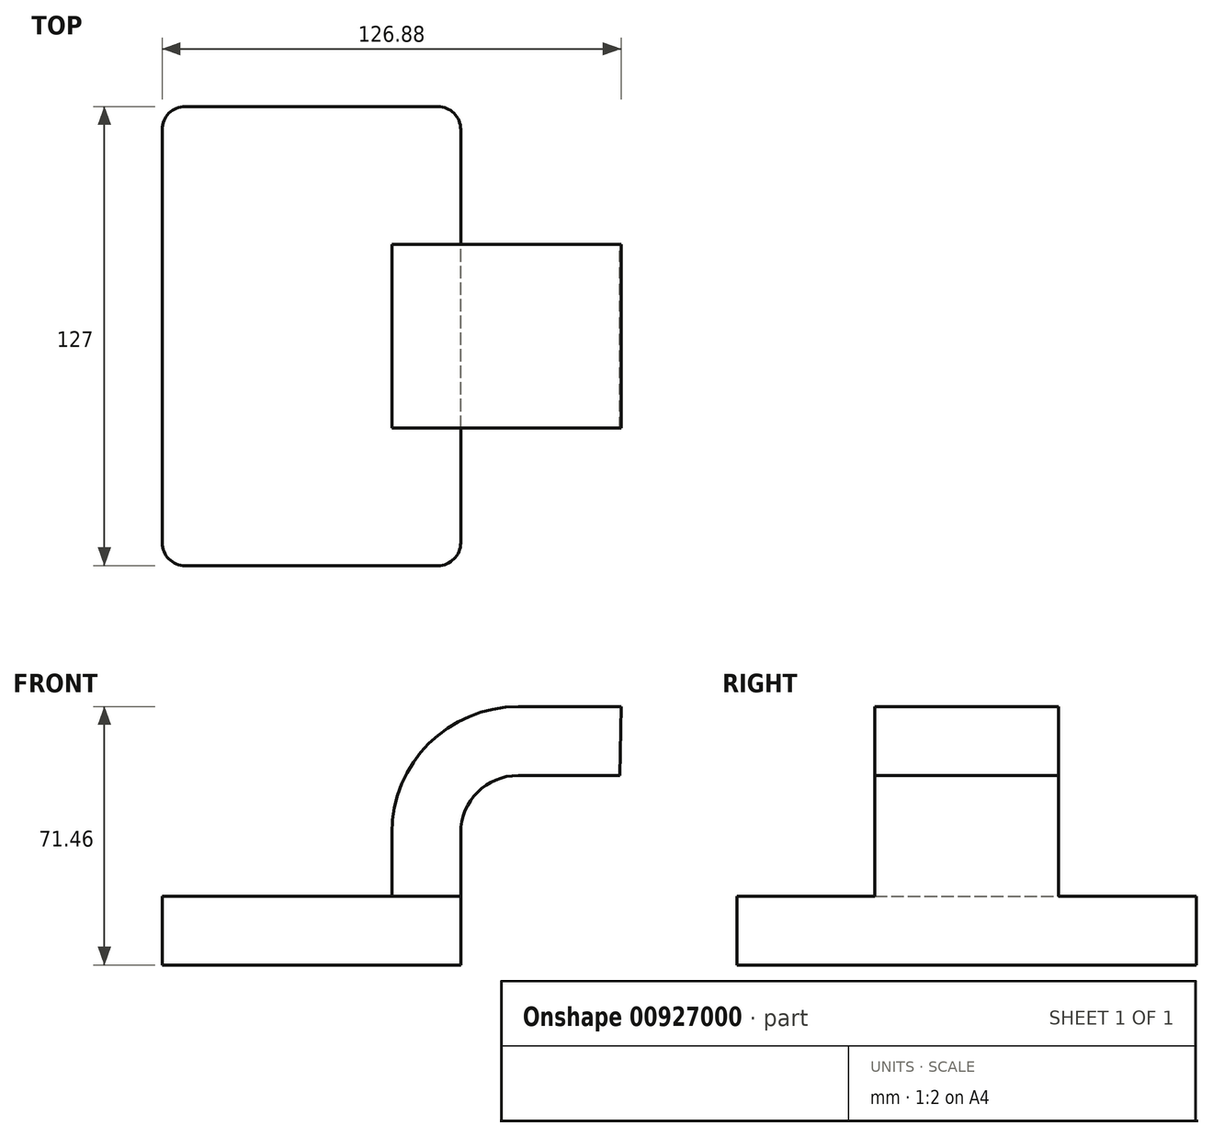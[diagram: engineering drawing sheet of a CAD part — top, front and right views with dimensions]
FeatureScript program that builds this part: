
annotation { "Feature Type Name" : "Feature", "Feature Type Description" : "" }
export const myFeature = defineFeature(function(context is Context, id is Id, definition is map)
    precondition{}
    {
        {
            var Q0;
            Q0=qCreatedBy(makeId("Front.planeOp"),FACE);
            var sketch = newSketch(context, id + "F0", { "sketchPlane" : qUnion([Q0])});
            skLineSegment(sketch, "E0.bottom", {"start": v(41.28, -9.52) * mm, "end": v(-41.27, -9.52) * mm});
            skLineSegment(sketch, "E0.top", {"start": v(41.27, 9.53) * mm, "end": v(-41.28, 9.53) * mm});
            skLineSegment(sketch, "E0.left", {"start": v(41.28, -9.52) * mm, "end": v(41.28, 9.53) * mm});
            skLineSegment(sketch, "E0.right", {"start": v(-41.27, -9.52) * mm, "end": v(-41.28, 9.53) * mm});
            skPoint(sketch, "E0.middle", {"position": v(0, 0) * mm});
            skLineSegment(sketch, "E1.bottom", {"start": v(111.12, 38.1) * mm, "end": v(60.33, 38.1) * mm});
            skLineSegment(sketch, "E1.top", {"start": v(111.12, 66.68) * mm, "end": v(60.33, 66.68) * mm});
            skLineSegment(sketch, "E1.left", {"start": v(111.12, 38.1) * mm, "end": v(111.12, 66.68) * mm});
            skLineSegment(sketch, "E1.right", {"start": v(60.33, 38.1) * mm, "end": v(60.33, 66.68) * mm});
            skPoint(sketch, "E1.middle", {"position": v(85.72, 52.39) * mm});
            skLineSegment(sketch, "E2", {"start": v(41.27, 9.53) * mm, "end": v(41.27, 27) * mm});
            skArc(sketch, "E3", {"start": v(41.28, 27) * mm, "mid": v(45.92, 38.23) * mm, "end": v(57.15, 42.88) * mm});
            skLineSegment(sketch, "E4", {"start": v(57.15, 42.88) * mm, "end": v(85.2, 42.88) * mm});
            skLineSegment(sketch, "E5.0", {"start": v(57.15, 61.93) * mm, "end": v(85.61, 61.93) * mm});
            skArc(sketch, "E5.1", {"start": v(22.23, 27) * mm, "mid": v(32.45, 51.7) * mm, "end": v(57.15, 61.93) * mm});
            skLineSegment(sketch, "E5.2", {"start": v(22.22, 9.53) * mm, "end": v(22.22, 27) * mm});
            skLineSegment(sketch, "E6", {"start": v(85.2, 42.88) * mm, "end": v(85.61, 61.93) * mm});
            skFitSpline(sketch, "E7", {"points": [v(-41.28, 9.52) * mm, v(57.15, 61.93) * mm], "startDerivative": vector(1.97, 111.4) * mm, "endDerivative": vector(217.07, -1.7) * mm});
            skSolve(sketch);
        }
        {
            var Q0;
            Q0=makeQuery(id+"F0.imprint","IMPRINT",FACE,{"disambiguationData":[TD([[makeQuery(id+"F0.imprint","IMPRINT",EDGE,{"derivedFrom":sQuery(id+"F0.wireOp",EDGE,"E0.bottom")}),-1.0]])]});
            extrude(context, id + "F1", {"entities" : qUnion([Q0]), "endBound" : BoundingType.SYMMETRIC, "depth" : 127 * mm, "offsetDistance" : 25.4 * mm});
        }
        {
            var Q0;
            {var subQ1=sQuery(id+"F0.wireOp",EDGE,"E2");Q0=makeQuery(id+"F0.imprint","IMPRINT",FACE,{"disambiguationData":[TD([[makeQuery(id+"F0.imprint","IMPRINT",EDGE,{"derivedFrom":subQ1}),1.0]])]});}
            var Q1;
            {var subQ5=sQuery(id+"F0.wireOp",EDGE,"E6");Q1=makeQuery(id+"F0.imprint","IMPRINT",FACE,{"disambiguationData":[TD([[makeQuery(id+"F0.imprint","IMPRINT",EDGE,{"derivedFrom":subQ5}),1.0]])]});}
            extrude(context, id + "F2", {"entities" : qUnion([Q0, Q1]), "operationType" : NewBodyOperationType.ADD, "endBound" : BoundingType.SYMMETRIC, "depth" : 50.8 * mm, "offsetDistance" : 25.4 * mm});
        }
        {
            var Q0;
            Q0=makeQuery(id+"F0.imprint","IMPRINT",FACE,{"disambiguationData":[TD([[makeQuery(id+"F0.imprint","IMPRINT",EDGE,{"derivedFrom":sQuery(id+"F0.wireOp",EDGE,"E5.1")}),1.0]])]});
            extrude(context, id + "F3", {"entities" : qUnion([Q0]), "operationType" : NewBodyOperationType.ADD, "endBound" : BoundingType.SYMMETRIC, "depth" : 15.24 * mm, "offsetDistance" : 25.4 * mm});
        }
        {
            var Q0;
            Q0=makeQuery(id+"F1.opExtrude","CAP_EDGE",EDGE,{"disambiguationData":[OSD([sQuery(id+"F0.wireOp",EDGE,"E0.left")])],"isStart":false});
            var Q1;
            Q1=makeQuery(id+"F1.opExtrude","CAP_EDGE",EDGE,{"disambiguationData":[OSD([sQuery(id+"F0.wireOp",EDGE,"E0.left")])],"isStart":true});
            var Q2;
            Q2=makeQuery(id+"F1.opExtrude","CAP_EDGE",EDGE,{"disambiguationData":[OSD([sQuery(id+"F0.wireOp",EDGE,"E0.right")])],"isStart":false});
            var Q3;
            Q3=makeQuery(id+"F1.opExtrude","CAP_EDGE",EDGE,{"disambiguationData":[OSD([sQuery(id+"F0.wireOp",EDGE,"E0.right")])],"isStart":true});
            fillet(context, id + "F4", {"entities" : qUnion([Q0, Q1, Q2, Q3]), "radius" : 6.35 * mm, "tangentPropagation" : true, "allowEdgeOverflow" : false});
        }
    });
